# Revit family: LEGRAND_NON INTERLOCKED SOCKETS_FLUSH MOUNTED_IP66_110
name_source: partatom
category: Installations électriques
revit_build: Autodesk Revit 2018 (Build: 20170223_1515(x64)
units: mm (PartAtom-declared; Revit-internal decimal feet)

## family parameters
Conserver l'orientation des annotations = Non
Cote de connecteur circulaire = Utiliser le diamètre
Couper avec des vides une fois chargée = Non
Hôte = Face
Partagée = Non
Point de calcul de pièce = Non
Type d'élément = Normal

## types (1)
- panel mounting socket IP66/67-55   16A   110 V   2P+E   plast
    Description = international standard socket for flush or surface mounting with accessory allows the connection of power devices
    Dia bouchon = 68 mm
    Elévation par défaut = 1000 mm  [stored 3.28084 ft]
    Fabricant = Legrand
    Flush E or Surface mounting S = flush and surface mounting
    General Conditions of Use = https://export.legrand.com
    Maximum installation temperature = 40°C
    Maximum use temperature = 100°C
    Minimum installation temperature = -20°C
    Minimum use temperature = -50°C
    Modèle = 051125
    Number of poles = 3
    Position of earth h = 4
    RAY BOUCHON = 34 mm
    Ray = 21 mm  [stored 0.0688976 ft]
    Standard IEC or NFC = IEC
    Tension V = 110 V  50/60 Hz yellow
    characteristic color = yellow
    connecting type = screw terminals
    dIA = 42 mm
    depth for flush mounting mm = 40 mm
    depth mm = 85 mm
    h1 = 43 mm
    halogen free = Non
    height mm = 72 mm
    horizontal fixing distance mm = 52 mm
    intensity A = 16 A
    material of box = plastic
    protection class IP = IP66/67-55
    resistance to chocks IK = 09
    vertical fixing distance mm = 60 mm
    width mm = 64 mm

note: [stored X ft] marks values corroborated as IEEE doubles in the binary element streams (Revit-internal decimal feet)
